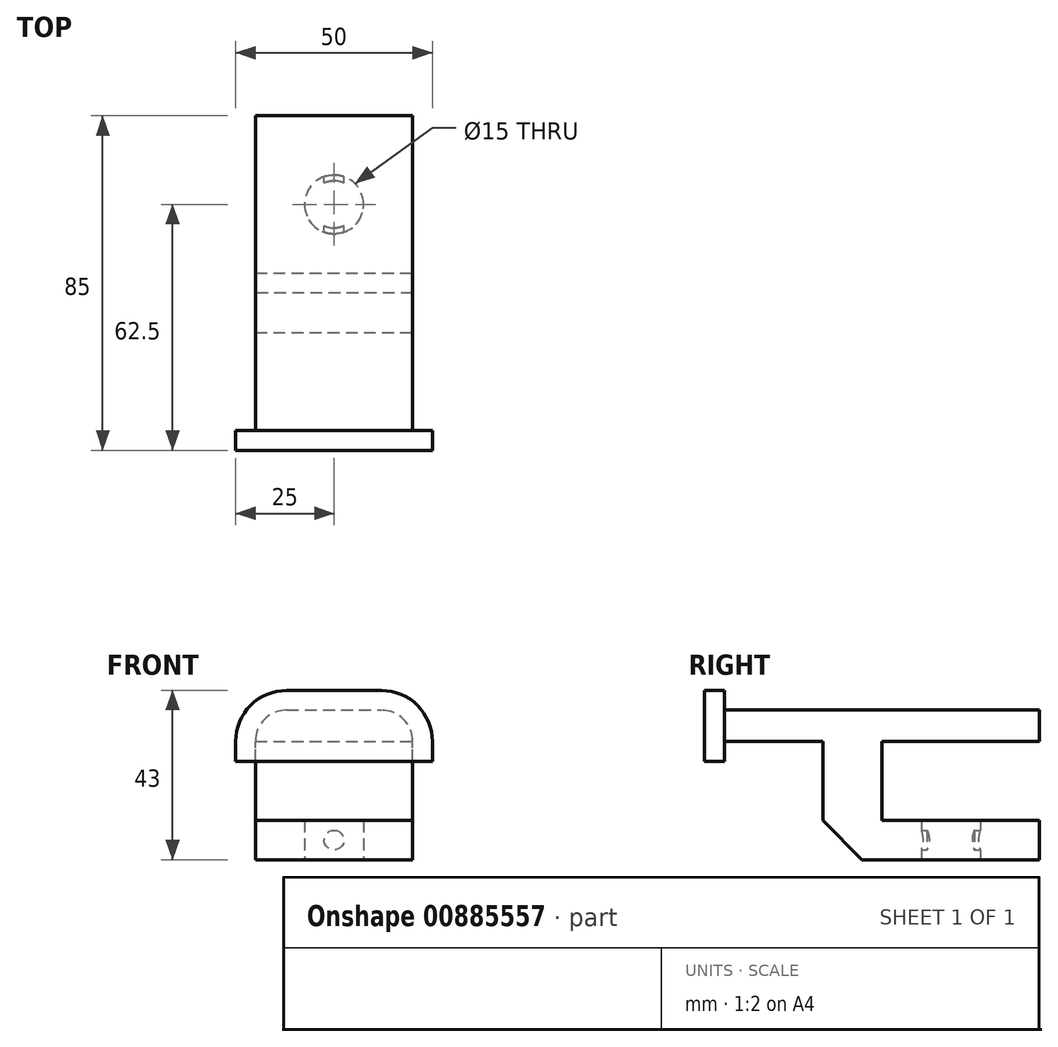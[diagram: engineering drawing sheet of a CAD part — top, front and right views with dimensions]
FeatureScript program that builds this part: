
annotation { "Feature Type Name" : "Feature", "Feature Type Description" : "" }
export const myFeature = defineFeature(function(context is Context, id is Id, definition is map)
    precondition{}
    {
        {
            var Q0;
            Q0=qCreatedBy(makeId("Top.planeOp"),FACE);
            var sketch = newSketch(context, id + "F0", { "sketchPlane" : qUnion([Q0])});
            skLineSegment(sketch, "E0.bottom", {"start": v(-40, -37.9) * mm, "end": v(0, -37.9) * mm});
            skLineSegment(sketch, "E0.top", {"start": v(-40, 42.1) * mm, "end": v(0, 42.1) * mm});
            skLineSegment(sketch, "E0.left", {"start": v(-40, -37.9) * mm, "end": v(-40, 42.1) * mm});
            skLineSegment(sketch, "E0.right", {"start": v(0, -37.9) * mm, "end": v(0, 42.1) * mm});
            skSolve(sketch);
        }
        {
            var Q0;
            Q0=qSketchRegion(id+"F0",true);
            extrude(context, id + "F1", {"entities" : qUnion([Q0]), "depth" : 8 * mm, "offsetDistance" : 25 * mm});
        }
        {
            var Q0;
            Q0=makeQuery(id+"F1.opExtrude","CAP_FACE",FACE,{"disambiguationData":[OSD([sQuery(id+"F0.wireOp",EDGE,"E0.bottom"),sQuery(id+"F0.wireOp",EDGE,"E0.top"),sQuery(id+"F0.wireOp",EDGE,"E0.left"),sQuery(id+"F0.wireOp",EDGE,"E0.right")])],"isStart":true});
            var sketch = newSketch(context, id + "F2", { "sketchPlane" : qUnion([Q0])});
            skLineSegment(sketch, "E1.bottom", {"start": v(-40, 37.9) * mm, "end": v(0, 37.9) * mm});
            skLineSegment(sketch, "E1.top", {"start": v(-40, -2.1) * mm, "end": v(0, -2.1) * mm});
            skLineSegment(sketch, "E1.left", {"start": v(-40, 37.9) * mm, "end": v(-40, -2.1) * mm});
            skLineSegment(sketch, "E1.right", {"start": v(0, 37.9) * mm, "end": v(0, -2.1) * mm});
            skLineSegment(sketch, "E2.top", {"start": v(-40, 12.9) * mm, "end": v(0, 12.9) * mm});
            skLineSegment(sketch, "E2.left", {"start": v(-40, -2.1) * mm, "end": v(-40, 12.9) * mm});
            skLineSegment(sketch, "E2.right", {"start": v(0, -2.1) * mm, "end": v(0, 12.9) * mm});
            skSolve(sketch);
        }
        {
            var Q0;
            {var subQ0=sQuery(id+"F2.wireOp",EDGE,"E1.top");Q0=makeQuery(id+"F2.imprint","IMPRINT",FACE,{"disambiguationData":[TD([[makeQuery(id+"F2.imprint","IMPRINT",EDGE,{"derivedFrom":subQ0}),1.0]])]});}
            extrude(context, id + "F3", {"entities" : qUnion([Q0]), "operationType" : NewBodyOperationType.ADD, "depth" : 30 * mm, "offsetDistance" : 25 * mm});
        }
        {
            var Q0;
            Q0=makeQuery(id+"F3.opExtrude","SWEPT_FACE",FACE,{"disambiguationData":[OSD([sQuery(id+"F2.wireOp",EDGE,"E1.top")])]});
            var sketch = newSketch(context, id + "F4", { "sketchPlane" : qUnion([Q0])});
            skLineSegment(sketch, "E3.bottom", {"start": v(0, -30) * mm, "end": v(40, -30) * mm});
            skLineSegment(sketch, "E3.top", {"start": v(0, -20) * mm, "end": v(40, -20) * mm});
            skLineSegment(sketch, "E3.left", {"start": v(0, -30) * mm, "end": v(0, -20) * mm});
            skLineSegment(sketch, "E3.right", {"start": v(40, -30) * mm, "end": v(40, -20) * mm});
            skSolve(sketch);
        }
        {
            var Q0;
            Q0=qSketchRegion(id+"F4",true);
            extrude(context, id + "F5", {"entities" : qUnion([Q0]), "operationType" : NewBodyOperationType.ADD, "depth" : 40 * mm, "offsetDistance" : 25 * mm});
        }
        {
            var Q0;
            Q0=makeQuery(id+"F1.opExtrude","CAP_EDGE",EDGE,{"disambiguationData":[OSD([sQuery(id+"F0.wireOp",EDGE,"E0.right")])],"isStart":false});
            var Q1;
            Q1=makeQuery(id+"F1.opExtrude","CAP_EDGE",EDGE,{"disambiguationData":[OSD([sQuery(id+"F0.wireOp",EDGE,"E0.left")])],"isStart":false});
            fillet(context, id + "F6", {"entities" : qUnion([Q0, Q1]), "radius" : 8 * mm, "tangentPropagation" : true, "allowEdgeOverflow" : false});
        }
        {
            var Q0;
            Q0=makeQuery(id+"F3.opExtrude","CAP_EDGE",EDGE,{"disambiguationData":[OSD([sQuery(id+"F2.wireOp",EDGE,"E2.top")])],"isStart":false});
            chamfer(context, id + "F7", {"entities" : qUnion([Q0]), "chamferType" : ChamferType.TWO_OFFSETS, "width1" : 10 * mm, "oppositeDirection" : true, "width2" : 10 * mm, "tangentPropagation" : true});
        }
        {
            var Q0;
            Q0=makeQuery(id+"F1.opExtrude","SWEPT_FACE",FACE,{"disambiguationData":[OSD([sQuery(id+"F0.wireOp",EDGE,"E0.bottom")])]});
            var sketch = newSketch(context, id + "F8", { "sketchPlane" : qUnion([Q0])});
            skArc(sketch, "E4.0", {"start": v(4, -5) * mm, "mid": v(2.82, 7.21) * mm, "end": v(-8, 13) * mm});
            skLineSegment(sketch, "E4.1", {"start": v(-44, -5) * mm, "end": v(4, -5) * mm});
            skArc(sketch, "E4.2", {"start": v(-32, 13) * mm, "mid": v(-42.82, 7.21) * mm, "end": v(-44, -5) * mm});
            skLineSegment(sketch, "E5", {"start": v(-32, 13) * mm, "end": v(-8, 13) * mm});
            skSolve(sketch);
        }
        {
            var Q0;
            Q0 = qSketchRegion(id + "F8", true);
            extrude(context, id + "F9", {"entities" : qUnion([Q0]), "operationType" : NewBodyOperationType.ADD, "depth" : 5 * mm, "offsetDistance" : 25 * mm});
        }
        {
            var Q0;
            Q0=makeQuery(id+"F9.opExtrude","SWEPT_FACE",FACE,{"disambiguationData":[OSD([sQuery(id+"F8.wireOp",EDGE,"E4.1")])]});
            var sketch = newSketch(context, id + "F10", { "sketchPlane" : qUnion([Q0])});
            skLineSegment(sketch, "E6.bottom", {"start": v(-44, 37.9) * mm, "end": v(4, 37.9) * mm});
            skLineSegment(sketch, "E6.top", {"start": v(-44, 42.9) * mm, "end": v(4, 42.9) * mm});
            skLineSegment(sketch, "E6.left", {"start": v(-44, 37.9) * mm, "end": v(-44, 42.9) * mm});
            skLineSegment(sketch, "E6.right", {"start": v(4, 37.9) * mm, "end": v(4, 42.9) * mm});
            skLineSegment(sketch, "E7.bottom", {"start": v(4, 42.9) * mm, "end": v(5, 42.9) * mm});
            skLineSegment(sketch, "E7.top", {"start": v(4, 37.9) * mm, "end": v(5, 37.9) * mm});
            skLineSegment(sketch, "E7.left", {"start": v(4, 42.9) * mm, "end": v(4, 37.9) * mm});
            skLineSegment(sketch, "E7.right", {"start": v(5, 42.9) * mm, "end": v(5, 37.9) * mm});
            skLineSegment(sketch, "E8.bottom", {"start": v(-44, 42.9) * mm, "end": v(-45, 42.9) * mm});
            skLineSegment(sketch, "E8.top", {"start": v(-44, 37.9) * mm, "end": v(-45, 37.9) * mm});
            skLineSegment(sketch, "E8.left", {"start": v(-44, 42.9) * mm, "end": v(-44, 37.9) * mm});
            skLineSegment(sketch, "E8.right", {"start": v(-45, 42.9) * mm, "end": v(-45, 37.9) * mm});
            skSolve(sketch);
        }
        {
            var Q0;
            Q0 = qSketchRegion(id + "F10", true);
            extrude(context, id + "F11", {"entities" : qUnion([Q0]), "operationType" : NewBodyOperationType.ADD, "oppositeDirection" : true, "depth" : 5 * mm, "offsetDistance" : 25 * mm});
        }
        {
            var Q0;
            Q0=makeQuery(id+"F5.boolean.opBoolean","MERGE",FACE,{"derivedFrom":[makeQuery(id+"F3.opExtrude","CAP_FACE",FACE,{"disambiguationData":[OSD([sQuery(id+"F2.wireOp",EDGE,"E1.top"),sQuery(id+"F2.wireOp",EDGE,"E1.left"),sQuery(id+"F2.wireOp",EDGE,"E1.right"),sQuery(id+"F2.wireOp",EDGE,"E2.top")])],"isStart":false}),makeQuery(id+"F5.opExtrude","SWEPT_FACE",FACE,{"disambiguationData":[OSD([sQuery(id+"F4.wireOp",EDGE,"E3.bottom")])]})]});
            var sketch = newSketch(context, id + "F12", { "sketchPlane" : qUnion([Q0])});
            skCircle(sketch, "E9", {"center": v(-20, -19.6) * mm, "radius": 7.5 * mm});
            skCircle(sketch, "E10", {"center": v(-20, -19.6) * mm, "radius": 6 * mm});
            skSolve(sketch);
        }
        {
            var Q0;
            Q0=makeQuery(id+"F12.imprint","IMPRINT",FACE,{"disambiguationData":[TD([[makeQuery(id+"F12.imprint","IMPRINT",EDGE,{"derivedFrom":sQuery(id+"F12.wireOp",EDGE,"E9")}),1.0]])]});
            var Q1;
            Q1=makeQuery(id+"F12.imprint","IMPRINT",FACE,{"disambiguationData":[TD([[makeQuery(id+"F12.imprint","IMPRINT",EDGE,{"derivedFrom":sQuery(id+"F12.wireOp",EDGE,"E10")}),1.0]])]});
            var Q2;
            Q2=sQuery(id+"F12.wireOp",EDGE,"E9");
            extrude(context, id + "F13", {"entities" : qUnion([Q0, Q1]), "operationType" : NewBodyOperationType.REMOVE, "surfaceEntities" : qUnion([Q2]), "oppositeDirection" : true, "depth" : 11 * mm, "offsetDistance" : 25 * mm});
        }
        {
            var Q0;
            Q0=makeQuery(id+"F5.opExtrude","CAP_FACE",FACE,{"disambiguationData":[OSD([sQuery(id+"F4.wireOp",EDGE,"E3.bottom"),sQuery(id+"F4.wireOp",EDGE,"E3.top"),sQuery(id+"F4.wireOp",EDGE,"E3.left"),sQuery(id+"F4.wireOp",EDGE,"E3.right")])],"isStart":false});
            var sketch = newSketch(context, id + "F14", { "sketchPlane" : qUnion([Q0])});
            skLineSegment(sketch, "E11", {"start": v(20, -30) * mm, "end": v(20, -20) * mm, "construction": true});
            skCircle(sketch, "E12", {"center": v(20, -25) * mm, "radius": 2.5 * mm});
            skSolve(sketch);
        }
        {
            var Q0;
            Q0 = qSketchRegion(id + "F14", true);
            extrude(context, id + "F15", {"entities" : qUnion([Q0]), "operationType" : NewBodyOperationType.ADD, "oppositeDirection" : true, "depth" : 32 * mm, "offsetDistance" : 25 * mm});
        }
        {
            var Q0;
            Q0=makeQuery(id+"F12.imprint","IMPRINT",FACE,{"disambiguationData":[TD([[makeQuery(id+"F12.imprint","IMPRINT",EDGE,{"derivedFrom":sQuery(id+"F12.wireOp",EDGE,"E10")}),1.0]])]});
            extrude(context, id + "F16", {"entities" : qUnion([Q0]), "operationType" : NewBodyOperationType.REMOVE, "oppositeDirection" : true, "depth" : 25 * mm, "offsetDistance" : 25 * mm});
        }
    });
